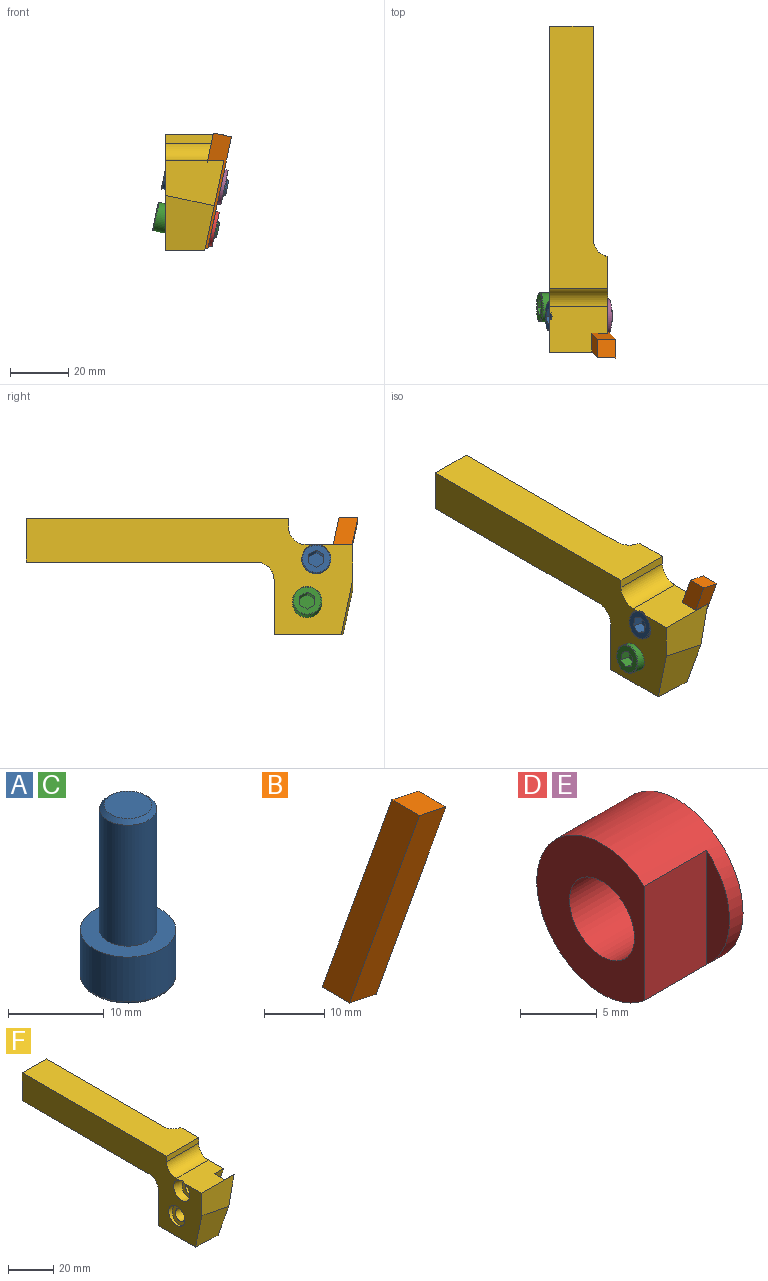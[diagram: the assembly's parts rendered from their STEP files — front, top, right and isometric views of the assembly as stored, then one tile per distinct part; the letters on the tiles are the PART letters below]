
ASSEMBLY  parts=6 mates=10
PART A: 14 faces, bbox 10.8x10.8x22 mm
  f0: plane 10x10mm, normal (0,0,1), area 50.3mm2, adj f1,f3
  f1: cylinder r=5mm len=10mm, axis (0,0,-1), area 180.6mm2, adj f0,f12
  f2: plane 9.5x9.5mm, normal (0,0,-1), area 47.5mm2, adj f5,f6,f7,f8,f9,f10,f12
  f3: cylinder r=3mm len=15.5mm, axis (0,0,-1), area 292.2mm2, adj f0,f13
  f4: plane 5x5mm, normal (0,0,1), area 19.6mm2, adj f13
  f5: plane 4x2.6mm, normal (0.87,-0.5,0), area 12mm2, adj f2,f6,f10,f11
  f6: plane 4x2.6mm, normal (0.87,0.5,0), area 12mm2, adj f2,f5,f7,f11
  f7: plane 4x3mm, normal (0,1,0), area 12mm2, adj f2,f6,f8,f11
  f8: plane 4x2.6mm, normal (-0.87,0.5,0), area 12mm2, adj f2,f7,f9,f11
  f9: plane 4x2.6mm, normal (-0.87,-0.5,0), area 12mm2, adj f2,f8,f10,f11
  f10: plane 4x3mm, normal (0,-1,0), area 12mm2, adj f2,f5,f9,f11
  f11: plane 6x5.2mm, normal (0,0,-1), area 23.4mm2, adj f5,f6,f7,f8,f9,f10
  f12: torus R=4.75mm, axis (0,0,1), area 12.1mm2, adj f1,f2
  f13: cone r=2.5mm half-angle=45deg, axis (0,0,-1), area 12.2mm2, adj f3,f4
PART B: 6 faces, bbox 14.3x14.8x39.6 mm
  f0: plane 39.59x14.35mm, normal (-0.04,-0.98,-0.2), area 254mm2, adj f1,f3,f4,f5
  f1: plane 6.49x6.21mm, normal (-0.21,0,-0.98), area 41.2mm2, adj f0,f2,f4,f5
  f2: plane 39.59x14.35mm, normal (0.04,0.98,0.2), area 254mm2, adj f1,f3,f4,f5
  f3: plane 6.49x6.21mm, normal (0.21,0,0.98), area 41.2mm2, adj f0,f2,f4,f5
  f4: plane 38.27x14.81mm, normal (0.98,0,-0.21), area 254mm2, adj f0,f1,f2,f3
  f5: plane 38.27x14.81mm, normal (-0.98,0,0.21), area 254mm2, adj f0,f1,f2,f3
PART C: same geometry as A
PART D: 6 faces, bbox 7x12x12 mm
  f0: cylinder r=6mm len=12mm, axis (1,0,0), area 204.3mm2, adj f2,f3,f4,f5
  f1: cylinder r=3mm len=7mm, axis (1,0,0), area 131.9mm2, adj f2,f3
  f2: plane 12x9.9mm, normal (-1,0,0), area 71.5mm2, adj f0,f1,f4
  f3: plane 12x12mm, normal (1,0,0), area 84.8mm2, adj f0,f1
  f4: plane 9.12x5.75mm, normal (0,-1,0), area 52.4mm2, adj f0,f2,f5
  f5: plane 9.12x2.1mm, normal (-1,0,0), area 13.3mm2, adj f0,f4
PART E: same geometry as D
PART F: 33 faces, bbox 22.4x112.3x40.3 mm
  f0: plane 31x6.75mm, normal (0.98,0,-0.21), area 80.6mm2, adj f1,f7,f8,f22,f32
  f1: plane 20x15.5mm, normal (0,-1,0), area 254.8mm2, adj f0,f8,f12,f32
  f2: plane 31.07x26.86mm, normal (0.98,0,-0.21), area 386.9mm2, adj f3,f5,f7,f8,f9,f13,f14,f15
  f3: plane 6.21x3.9mm, normal (-0.04,-0.98,-0.2), area 19.1mm2, adj f2,f7,f23,f28
  f4: cylinder r=3.1mm len=8.14mm, axis (0.98,0,-0.21), area 136.3mm2, adj f29,f31
  f5: plane 6.94x6.61mm, normal (-0.04,-0.98,-0.2), area 33.3mm2, adj f2,f23,f24,f28
  f6: cylinder r=3.1mm len=8.14mm, axis (0.98,0,-0.21), area 136.3mm2, adj f25,f27
  f7: plane 23.63x13.41mm, normal (0,0,-1), area 276.4mm2, adj f0,f2,f3,f12,f13,f22,f23,f32
  f8: plane 20x16mm, normal (0,0,1), area 282.2mm2, adj f0,f1,f2,f12,f17,f21,f22,f23
  f9: plane 17x9mm, normal (1,0,0), area 106.7mm2, adj f2,f11,f16,f17,f19
  f10: plane 15x15mm, normal (0,1,0), area 225mm2, adj f11,f12,f14,f18
  f11: plane 90x20mm, normal (0,0,1), area 1412.3mm2, adj f9,f10,f12,f16,f18,f19
  f12: plane 112.28x40.28mm, normal (-1,0,0), area 1974.4mm2, adj f1,f7,f8,f10,f11,f13,f14,f15
  f13: plane 19x17.45mm, normal (0,1,0), area 293.2mm2, adj f2,f7,f12,f15
  f14: plane 79x18.89mm, normal (0,0,-1), area 1192.1mm2, adj f2,f10,f12,f15,f18,f19,f20
  f15: cylinder r=6mm len=18.72mm, axis (1,0,0), area 172.1mm2, adj f2,f12,f13,f14
  f16: plane 20x3mm, normal (0,-1,0), area 60mm2, adj f9,f11,f12,f17
  f17: cylinder r=6mm len=20mm, axis (1,0,0), area 188.5mm2, adj f8,f9,f12,f16
  f18: plane 73.08x15mm, normal (1,0,0), area 1096.3mm2, adj f10,f11,f14,f19
  f19: cylinder r=6mm len=15mm, axis (0,0,-1), area 122.4mm2, adj f2,f9,f11,f14,f18,f20
  f20: plane 0.77x0.16mm, normal (0,-1,0), area 0.1mm2, adj f2,f14,f19
  f21: plane 6.51x5.34mm, normal (-0.04,-0.98,-0.2), area 27.4mm2, adj f2,f8,f23,f24
  f22: plane 31x12.21mm, normal (0.04,0.98,0.2), area 178.2mm2, adj f0,f7,f8,f23
  f23: plane 31x13.23mm, normal (0.98,0,-0.21), area 181mm2, adj f3,f5,f7,f8,f21,f22,f24,f28
  f24: cylinder r=6mm len=12.99mm, axis (0.98,0,-0.21), area 170.7mm2, adj f2,f5,f21,f23,f25
  f25: plane 12x11.74mm, normal (0.98,0,-0.21), area 82.9mm2, adj f6,f24
  f26: cylinder r=5mm len=11.15mm, axis (0.98,0,-0.21), area 171.9mm2, adj f8,f12,f27
  f27: plane 10x9.78mm, normal (-0.98,0,0.21), area 48.3mm2, adj f6,f26
  f28: cylinder r=6mm len=12.99mm, axis (0.98,0,-0.21), area 170.7mm2, adj f2,f3,f5,f23,f29
  f29: plane 12x11.74mm, normal (0.98,0,-0.21), area 82.9mm2, adj f4,f28
  f30: cylinder r=5mm len=10.51mm, axis (0.98,0,-0.21), area 75.9mm2, adj f12,f31
  f31: plane 10x9.78mm, normal (-0.98,0,0.21), area 48.3mm2, adj f4,f30
  f32: plane 19.05x16.71mm, normal (-0.04,-0.98,-0.2), area 268.9mm2, adj f0,f1,f7,f12
PLACE A rot(axis=(0.78,0,0.63),180deg) t=(-10.02,1.89,69.43)mm
PLACE B t=(4.56,124.49,38.32)mm
PLACE C rot(axis=(0.78,0,0.63),180deg) t=(-13.07,5.01,55.07)mm
PLACE D rot(axis=(0.71,0.71,-0.07),17deg) t=(17.3,75.39,8.21)mm
PLACE E rot(axis=(0.71,0.71,-0.07),17deg) t=(20.35,72.27,22.56)mm
PLACE F at identity fixed
MATE planar D.f5 <-> B.f4  axis (-0.98,0,0.21) through (15.7,10.98,6.7)mm
MATE planar F.f23 <-> B.f5  axis (0.98,0,-0.21) through (11.09,6.54,15.54)mm
MATE cylindrical F.f30 <-> D.f0  axis (0.98,0,-0.21) through (12.14,15.63,8.47)mm
MATE cylindrical F.f26 <-> E.f0  axis (0.98,0,-0.21) through (15.19,12.51,22.82)mm
MATE fastened C.f1 <-> F.f30  axis (0.98,0,-0.21) through (2.36,15.63,10.55)mm
MATE planar B.f0 <-> F.f22  axis (-0.04,-0.98,-0.2) through (15.42,2.37,20.64)mm
MATE planar E.f5 <-> B.f4  axis (-0.98,0,0.21) through (18.75,7.86,21.05)mm
MATE fastened A.f1 <-> F.f26  axis (0.98,0,-0.21) through (5.41,12.51,24.9)mm
MATE parallel D.f4 <-> B.f2  axis (-0.04,-0.98,-0.2) through (12.93,11.82,7.47)mm
MATE parallel E.f4 <-> B.f2  axis (-0.04,-0.98,-0.2) through (15.98,8.7,21.82)mm
